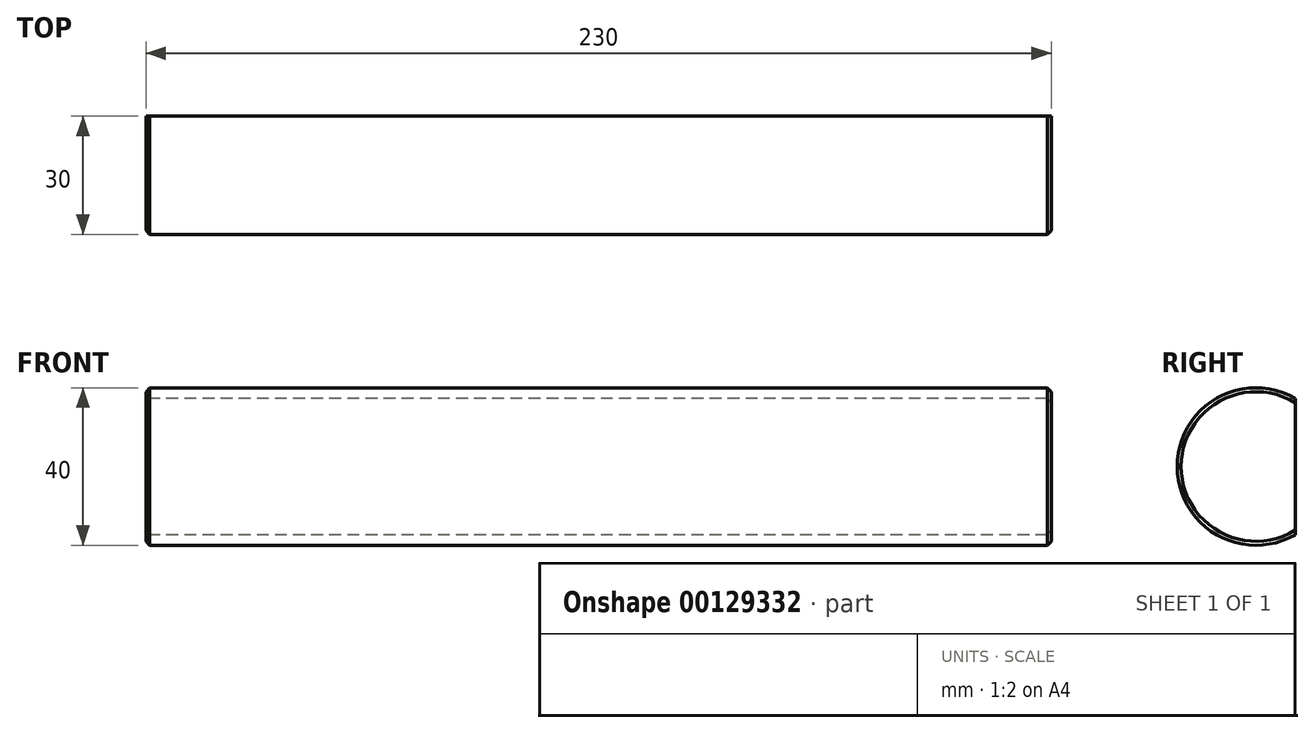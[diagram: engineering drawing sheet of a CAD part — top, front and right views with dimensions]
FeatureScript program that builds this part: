
annotation { "Feature Type Name" : "Feature", "Feature Type Description" : "" }
export const myFeature = defineFeature(function(context is Context, id is Id, definition is map)
    precondition{}
    {
        {
            var Q0;
            Q0=qCreatedBy(makeId("Right.planeOp"),FACE);
            var sketch = newSketch(context, id + "F0", { "sketchPlane" : qUnion([Q0])});
            skArc(sketch, "E0", {"start": v(10, 17.32) * mm, "mid": v(-20, 0) * mm, "end": v(10, -17.32) * mm});
            skLineSegment(sketch, "E1", {"start": v(10, 17.32) * mm, "end": v(10, -17.32) * mm});
            skPoint(sketch, "E2.orphan", {"position": v(10, 34.3) * mm});
            skSolve(sketch);
        }
        {
            var Q0;
            Q0=makeQuery(id+"F0.imprint","IMPRINT",FACE,{"disambiguationData":[TD([[makeQuery(id+"F0.imprint","IMPRINT",EDGE,{"derivedFrom":sQuery(id+"F0.wireOp",EDGE,"E0")}),1.0]])]});
            extrude(context, id + "F1", {"entities" : qUnion([Q0]), "depth" : 230 * mm});
        }
        {
            var Q0;
            Q0=makeQuery(id+"F1.opExtrude","CAP_EDGE",EDGE,{"disambiguationData":[OSD([sQuery(id+"F0.wireOp",EDGE,"E0")])],"isStart":true});
            var Q1;
            Q1=makeQuery(id+"F1.opExtrude","CAP_EDGE",EDGE,{"disambiguationData":[OSD([sQuery(id+"F0.wireOp",EDGE,"E0")])],"isStart":false});
            chamfer(context, id + "F2", {"entities" : qUnion([Q0, Q1]), "width" : 1 * mm, "tangentPropagation" : true});
        }
    });
